# Revit family: Shower-Valve_Trim-KALLISTA-Vice-P34889
name_source: partatom
category: Specialty Equipment
units: mm (PartAtom-declared; Revit-internal decimal feet)

## family parameters
Cut with Voids When Loaded = No
Host = Face
OmniClass Number = 23.31.25.00
OmniClass Title = Toilet and Bath Specialties
Part Type = Normal
Room Calculation Point = No
Round Connector Dimension = Use Diameter
Shared = No

## types (4) — shared parameters
ADA Compliant = No
Date Modified = 05/26/2024
Default Elevation = 42"
Description = Transfer TR M Wheel
Drain Included = No
Handle Clearance = 3 3/16"
Height = 4"
Length = 4 1/16"
Manufacturer = Kallista Co.
Master Format 2014 = 10 28 00
Master Format 2014 Name = Toilet, Bath, and Laundry Accessories
Material = Premium Metal Construction
Product Name = Vice
URL = https://www.kallista.com
WaterSense Certified = No
Width = 4"

## per-type parameters (varying)
| type | Assembly Code | Finish | Model | Type |
| AF-French Gold | C1030200 | Kallista-Metal-AF-French_Gold | P34889-00-AF | 1 |
| BGP | D2010700 | Kallista-Metal-BGP | P34889-00-BGP | 2 |
| CP-Chrome | D2010700 | Kallista-Metal-CP-Chrome | P34889-00-CP | 3 |
| SN-Polished Nickel | D2010700 | Kallista-Metal-SN-Polished_Nickel | P34889-00-SN | 4 |

## geometry (parser evidence)
native form markers: Sweep x5
no freeform markers — native parametric forms only
